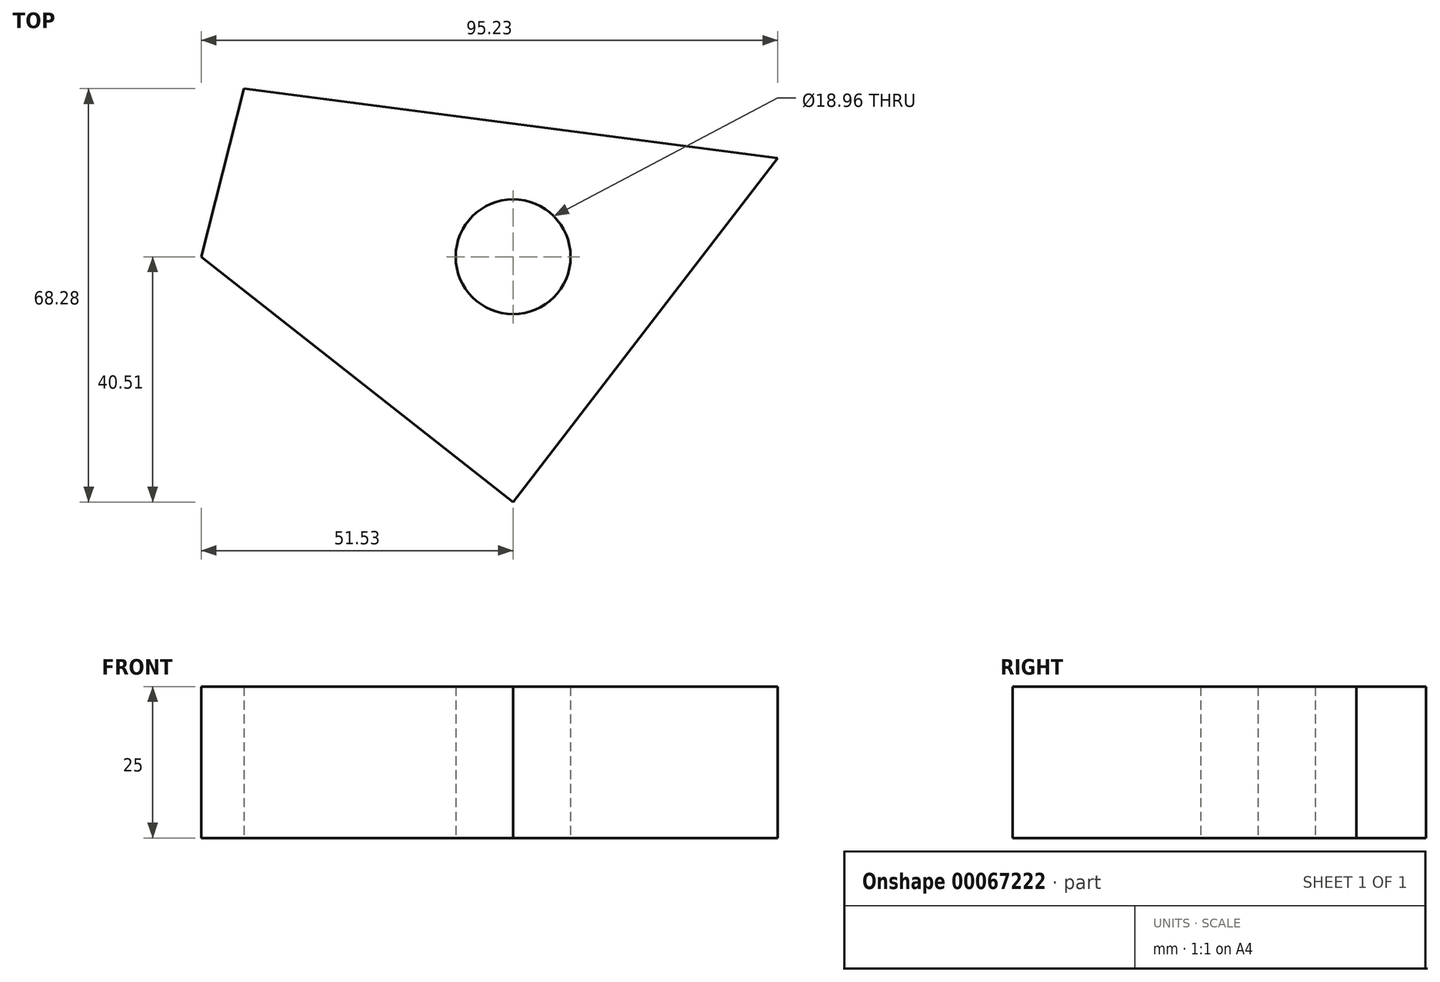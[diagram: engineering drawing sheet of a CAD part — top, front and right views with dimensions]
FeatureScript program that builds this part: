
annotation { "Feature Type Name" : "Feature", "Feature Type Description" : "" }
export const myFeature = defineFeature(function(context is Context, id is Id, definition is map)
    precondition{}
    {
        {
            var Q0;
            Q0=qCreatedBy(makeId("Top.planeOp"),FACE);
            var sketch = newSketch(context, id + "F0", { "sketchPlane" : qUnion([Q0])});
            skLineSegment(sketch, "E0", {"start": v(0, -40.51) * mm, "end": v(-51.53, 0) * mm});
            skLineSegment(sketch, "E1", {"start": v(-51.53, 0) * mm, "end": v(-44.43, 27.77) * mm});
            skLineSegment(sketch, "E2", {"start": v(-44.43, 27.77) * mm, "end": v(43.7, 16.3) * mm});
            skLineSegment(sketch, "E3", {"start": v(43.7, 16.3) * mm, "end": v(0, -40.51) * mm});
            skCircle(sketch, "E4", {"center": v(0, 0) * mm, "radius": 9.48 * mm});
            skSolve(sketch);
        }
        {
            var Q0;
            Q0 = qSketchRegion(id + "F0", true);
            extrude(context, id + "F1", {"entities" : qUnion([Q0]), "depth" : 25 * mm});
        }
    });
